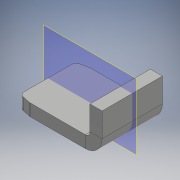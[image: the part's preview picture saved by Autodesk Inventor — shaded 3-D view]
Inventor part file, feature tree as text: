
AUTODESK INVENTOR PART (.ipt)
format: ipt  version: 2018 (Build 220112000, 112)  size: 135,168 bytes
history: native  units: mm
features: sheet_metal_op x4, other x3, sketch x2
ambient origin geometry x8: Origin, YZ Plane, XZ Plane, XY Plane, X Axis, Y Axis, Z Axis, Center Point
bodies: Solid1 (feature_tree)
feature tree (9):
  sheet_metal_op  "Face1"
  sheet_metal_op  "Flange1"
  other  "midtplan"
  sketch  "Sketch1"  dims[d2=2.094395mm d3=2.094395mm]
  other  "Plate1"
  sketch  "Sketch2"  dims[d4=25.0mm d5=2.094395mm d7=35.0mm d8=5.0mm d9=5.0mm d10=5.0mm d11=2.5mm d12=10.0mm d13=2.0mm d14=12.0mm d15=90.0deg d16=2.0mm d17=20.0mm d18=5.0mm d19=2.0mm d20=2.0mm]
  other  "Plate2"
  sheet_metal_op  "Bend1"
  sheet_metal_op  "Corner1"
